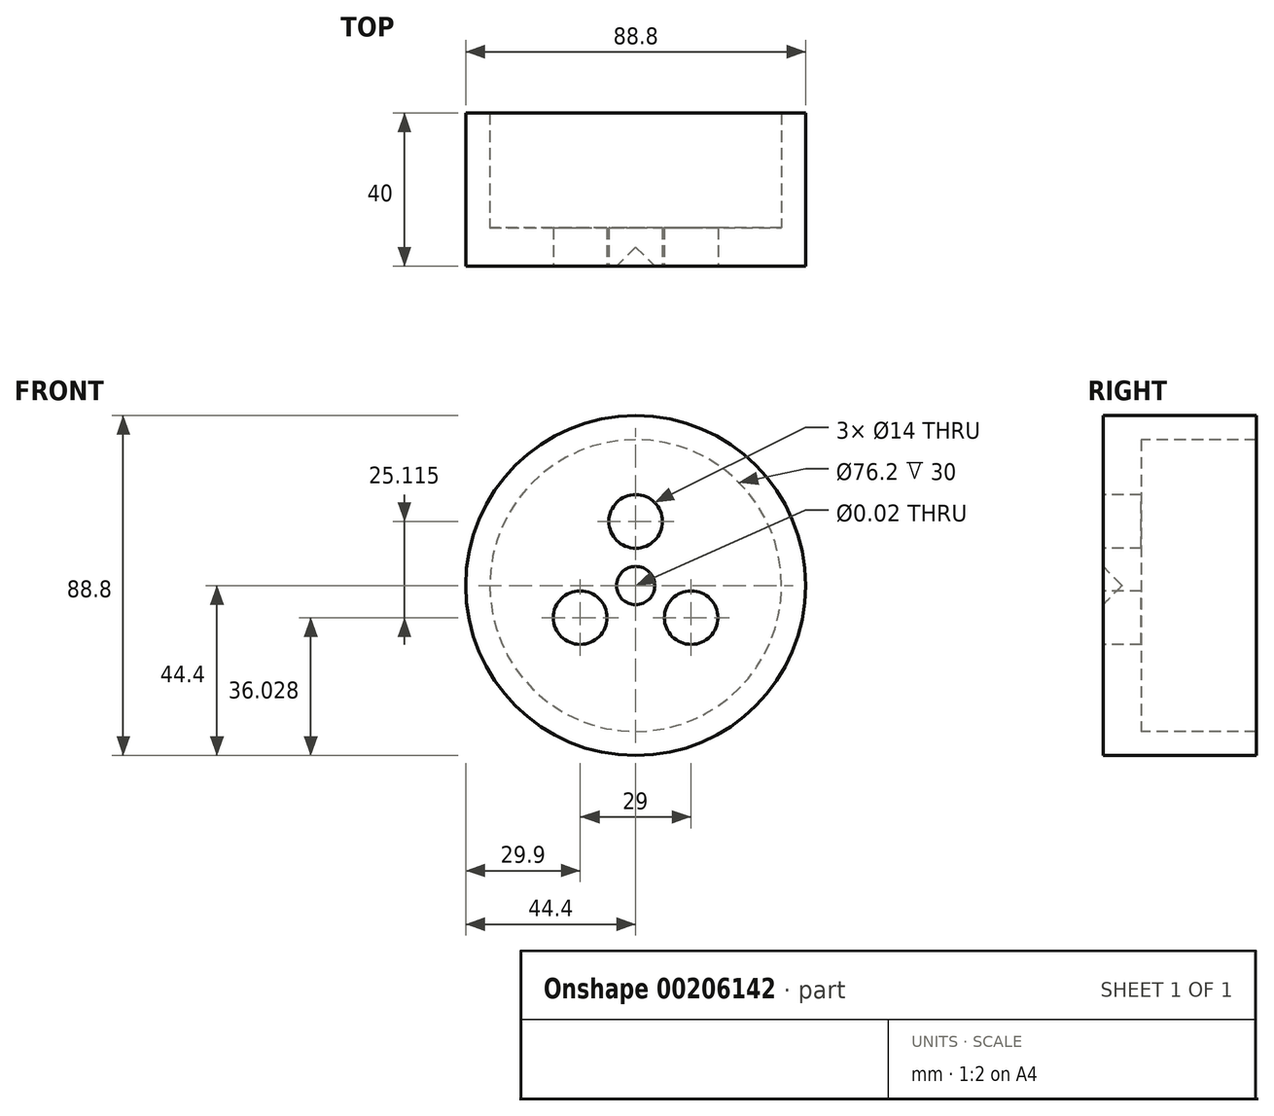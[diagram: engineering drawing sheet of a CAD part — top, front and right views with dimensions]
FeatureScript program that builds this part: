
annotation { "Feature Type Name" : "Feature", "Feature Type Description" : "" }
export const myFeature = defineFeature(function(context is Context, id is Id, definition is map)
    precondition{}
    {
        {
            var Q0;
            Q0=qCreatedBy(makeId("Front.planeOp"),FACE);
            var sketch = newSketch(context, id + "F0", { "sketchPlane" : qUnion([Q0])});
            skCircle(sketch, "E0", {"center": v(0, 0) * mm, "radius": 44.4 * mm});
            skSolve(sketch);
        }
        {
            var Q0;
            Q0 = qSketchRegion(id + "F0", true);
            extrude(context, id + "F1", {"entities" : qUnion([Q0]), "depth" : 10 * mm});
        }
        {
            var Q0;
            Q0=makeQuery(id+"F1.opExtrude","CAP_FACE",FACE,{"disambiguationData":[OSD([sQuery(id+"F0.wireOp",EDGE,"E0")])],"isStart":true});
            var sketch = newSketch(context, id + "F2", { "sketchPlane" : qUnion([Q0])});
            skCircle(sketch, "E1", {"center": v(0, 0) * mm, "radius": 38.1 * mm});
            skCircle(sketch, "E2", {"center": v(0, 0) * mm, "radius": 44.4 * mm});
            skSolve(sketch);
        }
        {
            var Q0;
            Q0 = qSketchRegion(id + "F2", true);
            extrude(context, id + "F3", {"entities" : qUnion([Q0]), "operationType" : NewBodyOperationType.ADD, "depth" : 30 * mm});
        }
        {
            var Q0;
            Q0=makeQuery(id+"F1.opExtrude","CAP_FACE",FACE,{"disambiguationData":[OSD([sQuery(id+"F0.wireOp",EDGE,"E0")])],"isStart":false});
            var sketch = newSketch(context, id + "F4", { "sketchPlane" : qUnion([Q0])});
            skCircle(sketch, "E3", {"center": v(0, 16.74) * mm, "radius": 7 * mm});
            skCircle(sketch, "E4.1.0", {"center": v(-14.5, -8.37) * mm, "radius": 7 * mm});
            skCircle(sketch, "E4.2.0", {"center": v(14.5, -8.37) * mm, "radius": 7 * mm});
            skPoint(sketch, "E4.center", {"position": v(0, 0) * mm});
            skSolve(sketch);
        }
        {
            var Q0;
            Q0 = qSketchRegion(id + "F4", true);
            extrude(context, id + "F5", {"entities" : qUnion([Q0]), "operationType" : NewBodyOperationType.REMOVE, "endBound" : BoundingType.THROUGH_ALL, "oppositeDirection" : true, "depth" : 25 * mm});
        }
        {
            var Q0;
            Q0=makeQuery(id+"F1.opExtrude","CAP_FACE",FACE,{"disambiguationData":[OSD([sQuery(id+"F0.wireOp",EDGE,"E0")])],"isStart":false});
            var sketch = newSketch(context, id + "F6", { "sketchPlane" : qUnion([Q0])});
            skPoint(sketch, "E5", {"position": v(0, 0) * mm});
            skSolve(sketch);
        }
        {
            var Q0;
            Q0=sQuery(id+"F6.wireOp",VERTEX,"E5");
            var Q1;
            Q1=makeQuery(id+"F1.opExtrude","SWEPT_BODY",BODY,{"disambiguationData":[OSD([sQuery(id+"F0.wireOp",EDGE,"E0")])]});
            hole(context, id + "F7", {"style" : HoleStyle.C_SINK, "endStyle" : HoleEndStyle.BLIND, "holeDiameter" : 0.02 * mm, "cSinkDiameter" : 10 * mm, "cSinkAngle" : 90 * degree, "holeDepth" : 5 * mm, "startFromSketch" : true, "locations" : qUnion([Q0]), "scope" : qUnion([Q1])});
        }
    });
